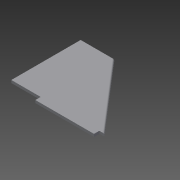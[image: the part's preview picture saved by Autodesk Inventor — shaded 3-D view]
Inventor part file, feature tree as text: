
AUTODESK INVENTOR PART (.ipt)
format: ipt  version: 2014 SP1 (Build 180222100, 222)  size: 81,408 bytes
history: native  units: mm
features: extrude x1, fillet x1, sketch x1
ambient origin geometry x8: Origin, YZ Plane, XZ Plane, XY Plane, X Axis, Y Axis, Z Axis, Center Point
bodies: Solid1 (feature_tree)
feature tree (3):
  extrude  "Extrusion1"  Depth=2.5mm
  fillet  "Fillet1"  Radius=175.0mm
  sketch  "Sketch1"  dims[d1=110.0mm d5=45.0mm d6=175.0mm d7=10.0mm d8=10.0mm d9=110.0mm d10=5.0mm d11=0.0mm d12=2.5mm]
